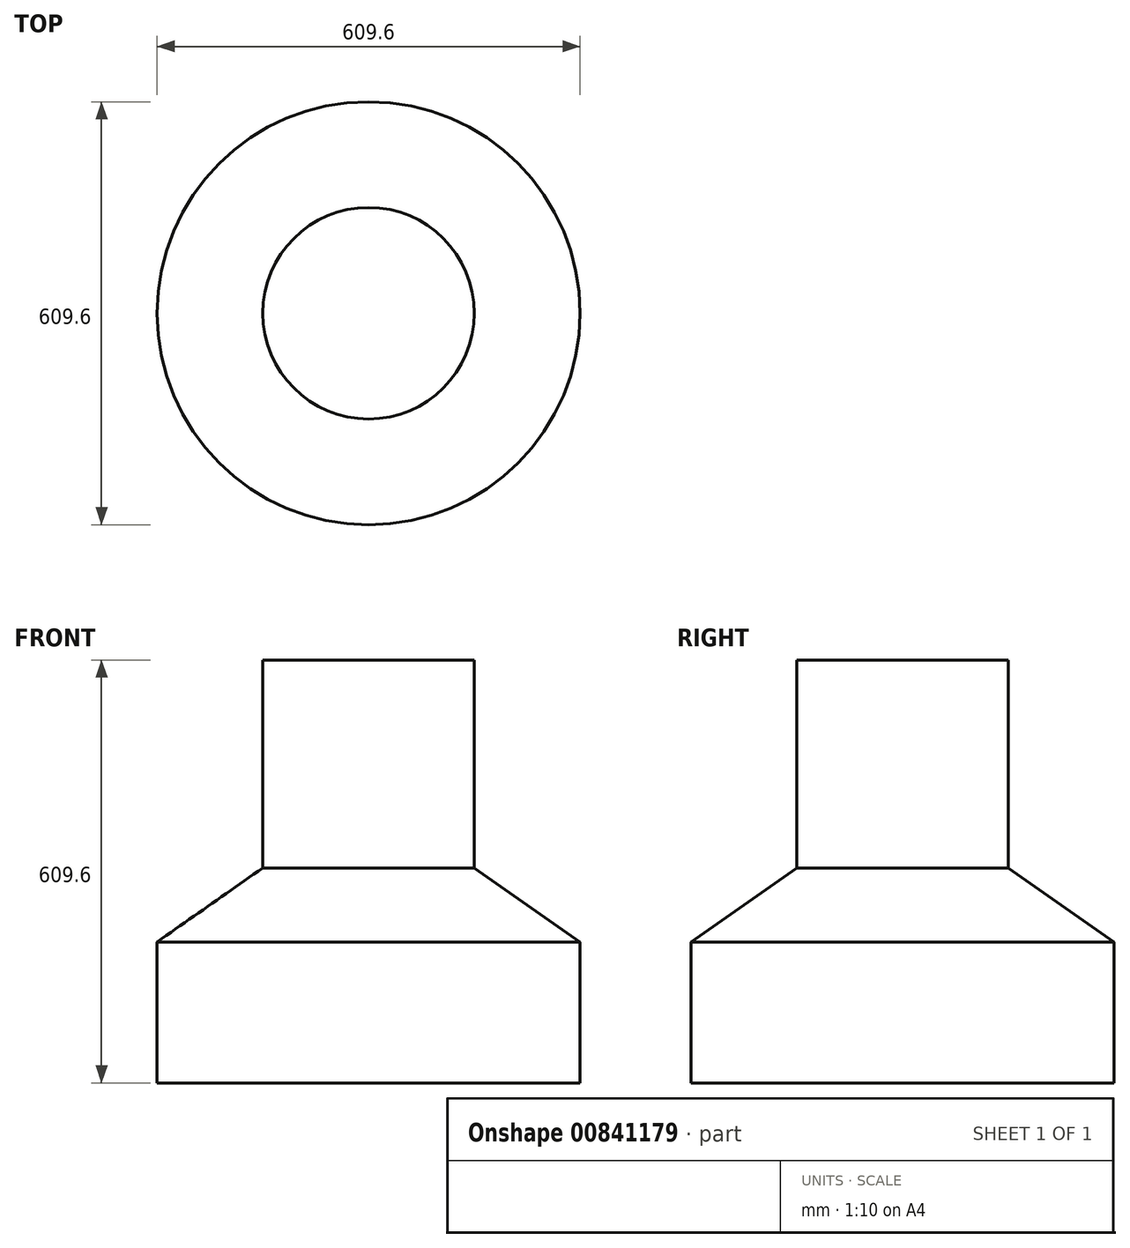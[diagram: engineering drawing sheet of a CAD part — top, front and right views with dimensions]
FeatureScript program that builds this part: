
annotation { "Feature Type Name" : "Feature", "Feature Type Description" : "" }
export const myFeature = defineFeature(function(context is Context, id is Id, definition is map)
    precondition{}
    {
        {
            var Q0;
            Q0=qCreatedBy(makeId("Front.planeOp"),FACE);
            var sketch = newSketch(context, id + "F0", { "sketchPlane" : qUnion([Q0])});
            skLineSegment(sketch, "E0", {"start": v(0, 406.4) * mm, "end": v(0, 106.71) * mm});
            skLineSegment(sketch, "E1", {"start": v(-152.4, 0) * mm, "end": v(-152.4, -203.2) * mm});
            skLineSegment(sketch, "E2", {"start": v(-152.4, -203.2) * mm, "end": v(152.4, -203.2) * mm});
            skLineSegment(sketch, "E3", {"start": v(152.4, -203.2) * mm, "end": v(152.4, 406.4) * mm});
            skLineSegment(sketch, "E4", {"start": v(152.4, 406.4) * mm, "end": v(0, 406.4) * mm});
            skLineSegment(sketch, "E5", {"start": v(-152.4, 0) * mm, "end": v(0, 106.71) * mm});
            skSolve(sketch);
        }
        {
            var Q0;
            Q0=makeQuery(id+"F0.imprint","IMPRINT",FACE,{"disambiguationData":[TD([[makeQuery(id+"F0.imprint","IMPRINT",EDGE,{"derivedFrom":sQuery(id+"F0.wireOp",EDGE,"E0")}),1.0]])]});
            var Q1;
            Q1=sQuery(id+"F0.wireOp",EDGE,"E3");
            revolve(context, id + "F1", {"surfaceOperationType" : NewSurfaceOperationType.NEW, "entities" : qUnion([Q0]), "axis" : qUnion([Q1]), "revolveType" : RevolveType.FULL});
        }
    });
